# Revit family: Skrz_metal_EI60_1_pn90,100
name_source: partatom
category: Drzwi
revit_build: Autodesk Revit 2016 (Build: 20150714_1515(x64)
units: mm (PartAtom-declared; Revit-internal decimal feet)

## family parameters
Numer OmniClass = 23.30.10.00
Obiekt nadrzędny = Ściana
Punkt obliczania pomieszczeń = Nie
Tnij formami wycięć po wczytaniu = Nie
Tytuł OmniClass = Doors
Współdzielony = Nie
Zawsze pionowo = Tak

## types (2) — shared parameters
Funkcja = Wewnętrzna
Informacja = Własność Porta KMI Poland, wszelkie prawa zastrzeżone.
Konstrukcja analityczna = <Brak>
Materiał klamka = <Wg kategorii>
Materiał ościeżnica = <Wg kategorii>
Materiał skrzydło = <Wg kategorii>
Materiał szklenie = Szkło
Model = Metalowe EI60
Producent = PORTA KMI Poland
Wysokość = 2029 mm
Zakończenie ściany = Wg obiektu nadrzędnego

## per-type parameters (varying)
| type | Szerokość | Szerokość brutto | Szerokość skrzydła | Wysokość brutto |
| 90 | 940 mm  [stored 3.08399 ft] | 1010 mm  [stored 3.31365 ft] | 1016 mm | 2064 mm  [stored 6.77165 ft] |
| 100 | 1040 mm | 1110 mm | 1116 mm | 2065 mm |

note: [stored X ft] marks values corroborated as IEEE doubles in the binary element streams (Revit-internal decimal feet)

## geometry (parser evidence)
native form markers: Blend x4
no freeform markers — native parametric forms only
